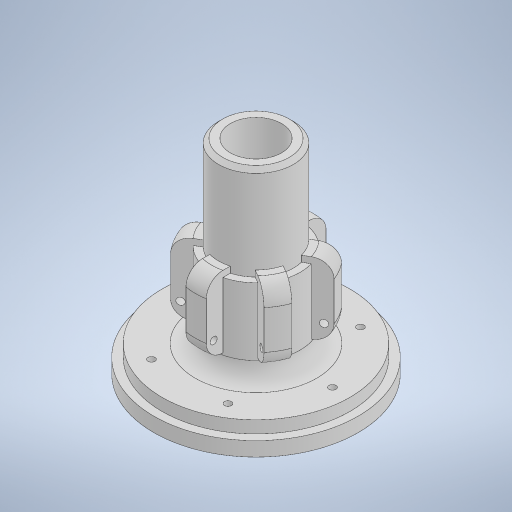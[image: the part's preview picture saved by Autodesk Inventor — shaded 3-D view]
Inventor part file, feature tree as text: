
AUTODESK INVENTOR PART (.ipt)
format: ipt  version: 2024.3 (Build 283343000, 343)  size: 481,280 bytes
history: native  units: mm
features: sketch x12, extrude x7, fillet x3, pattern_circular x3, hole x3, plane x2, projected_geometry x2, chamfer x1
ambient origin geometry x8: Origin, YZ Plane, XZ Plane, XY Plane, X Axis, Y Axis, Z Axis, Center Point
bodies: Solid1 (feature_tree)
feature tree (33):
  sketch  "Sketch1"  dims[d1=25.0mm d2=5.8mm]
  extrude  "Extrusion1"  Depth=5.8mm
  extrude  "Extrusion2"  Depth=100.0mm TaperAngle=0.0deg
  plane  "Work Plane1"
  extrude  "Extrusion3"  Depth=10.0mm
  sketch  "Sketch3"  dims[d8=31.0mm d23=15.0mm d24=10.0mm]
  fillet  "Fillet2"  Radius=10.0mm
  pattern_circular  "Circular Pattern1"  Count=6 Angle=360.0deg
  plane  "Plano de trabajo2"
  extrude  "Extrusión5"  Depth=50.0mm TaperAngle=0.0deg
  extrude  "Extrusión6"  Depth=8.0mm
  fillet  "Empalme4"  Radius=60.0mm
  pattern_circular  "Patrón circular2"  Count=6 Angle=360.0deg
  chamfer  "Chaflán1"  Distance=6.0mm
  sketch  "Boceto6"  dims[d31=3.0mm]
  extrude  "Extrusión8"  Depth=8.0mm TaperAngle=360.0deg
  fillet  "Empalme6"  Radius=37.5mm
  hole  "Agujero4"  [1 undecoded]
  pattern_circular  "Patrón circular3"  [2 undecoded]
  extrude  "Extrusión9"  Depth=8.0mm
  hole  "Agujero5"  [1 undecoded]
  hole  "Agujero6"  [1 undecoded]
  sketch  "Boceto13"  dims[d79=8.0mm d81=3.4mm d82=6.0mm d83=6.3mm d84=2.0mm d85=90.0deg d86=8.0mm d87=20.594885mm d88=60.0mm d89=360.0deg d91=37.5mm d92=25.74mm d94=4.0mm d95=0.0mm d97=31.0mm d98=7.5mm d99=2.459mm d100=9.0mm d101=4.0mm d102=2.0mm d103=90.0deg d104=9.0mm d105=120.0deg d106=30.0deg d107=37.5mm d108=60.0mm d110=360.0deg d112=3.4mm d113=6.0mm d114=4.0mm d115=2.0mm d116=90.0deg d117=8.0mm d118=20.594885mm d119=37.5mm d120=60.0mm d122=360.0deg d29=0.0mm d30=0.0mm d32=0.0mm d37=0.0mm]
  sketch  "Sketch2"  dims[d3=7.0mm d4=0.0mm d5=100.0mm d6=0.0mm]
  sketch  "Boceto4"  dims[d25=29.75mm]
  sketch  "Boceto5"  dims[d27=15.0mm d28=0.0mm]
  projected_geometry  "Contorno proyectado1"
  sketch  "Boceto8"  dims[d34=8.0mm d35=60.0mm d36=360.0deg]
  projected_geometry  "Contorno proyectado4"
  sketch  "Boceto9"  dims[d40=-46.0mm d42=50.0mm d43=0.0mm]
  sketch  "Boceto10"  dims[d45=20.0mm d46=0.0mm d47=8.0mm d48=60.0mm d49=360.0deg]
  sketch  "Boceto11"  dims[d51=2.0mm d52=2.0mm d53=45.0deg]
  sketch  "Boceto12"  dims[d54=43.5mm d71=60.0mm d73=360.0deg d77=6.0mm d78=0.0mm]
note: 5 required parameter values undecoded (feature->parameter linkage not recoverable at this tier; creation-order binding heuristic only, values carry confidence <= 0.55)
